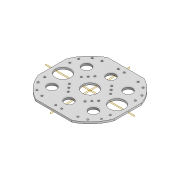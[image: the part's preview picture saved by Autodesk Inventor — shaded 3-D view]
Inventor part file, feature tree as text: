
AUTODESK INVENTOR PART (.ipt)
format: ipt  version: 2022 (Build 260153000, 153)  size: 234,496 bytes
history: native  units: mm
features: extrude x3, mirror x3, plane x2, sketch x2, projected_geometry x1
ambient origin geometry x8: Origin, YZ Plane, XZ Plane, XY Plane, X Axis, Y Axis, Z Axis, Center Point
bodies: Solid1 (feature_tree)
feature tree (11):
  extrude  "Extrusion1"  Depth=3.0mm TaperAngle=0.0deg
  extrude  "Extrusion3"  Depth=10.0mm
  plane  "Work Plane5"
  plane  "Work Plane6"
  mirror  "Mirror3"
  mirror  "Mirror4"
  extrude  "Extrusion4"  Depth=3.0mm
  mirror  "Mirror5"
  sketch  "Sketch10"  dims[d25=60.0mm d27=8.726646mm d28=3.0mm d30=3.0mm d32=25.0mm d33=62.0mm d34=8.0mm d35=8.0mm d36=10.0mm d37=0.0mm d38=63.0mm d39=63.0mm d40=3.0mm d41=25.0mm d42=3.0mm d43=3.0mm d44=8.0mm d45=8.0mm d46=4.95mm d47=4.95mm d48=100.0mm d49=0.0mm d50=3.0mm d51=10.0mm d52=25.0mm d53=45.0mm d54=15.0mm d55=35.0mm d56=15.0mm d57=45.0mm d58=25.0mm]
  sketch  "Sketch7"  dims[d0=120.0mm d2=3.0mm d3=0.0mm]
  projected_geometry  "Projected Loop6"
